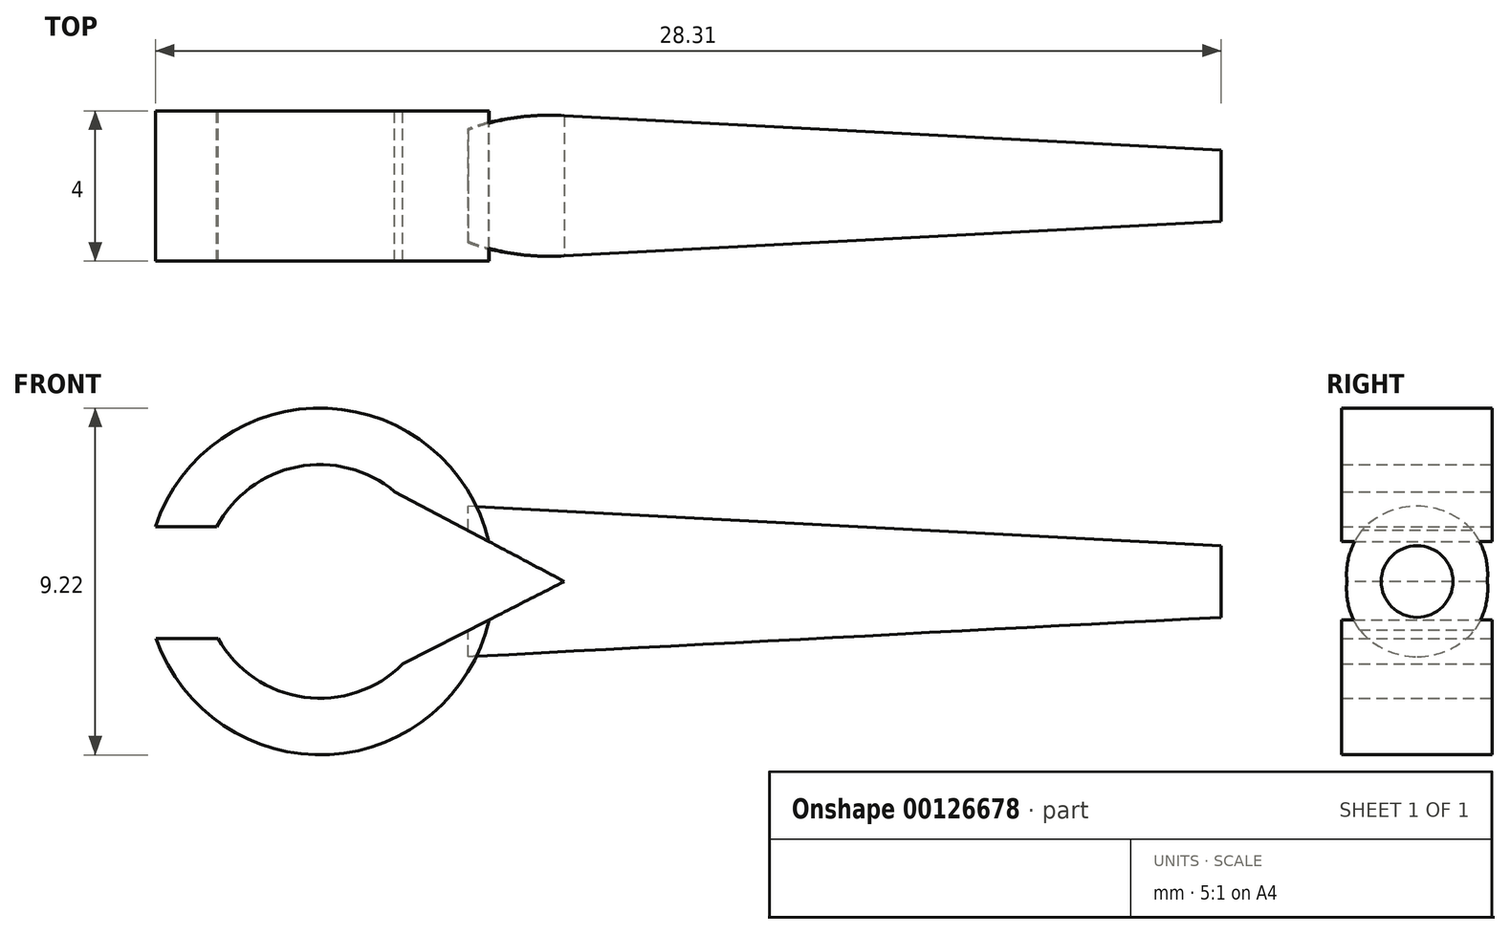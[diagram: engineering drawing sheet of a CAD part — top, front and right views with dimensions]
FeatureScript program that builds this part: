
annotation { "Feature Type Name" : "Feature", "Feature Type Description" : "" }
export const myFeature = defineFeature(function(context is Context, id is Id, definition is map)
    precondition{}
    {
        {
            var Q0;
            Q0=qCreatedBy(makeId("Front.planeOp"),FACE);
            var sketch = newSketch(context, id + "F0", { "sketchPlane" : qUnion([Q0])});
            skCircle(sketch, "E0", {"center": v(0, 0) * mm, "radius": 4.6 * mm});
            skCircle(sketch, "E1", {"center": v(0, 0) * mm, "radius": 3.1 * mm});
            skSolve(sketch);
        }
        {
            var Q0;
            Q0=makeQuery(id+"F0.imprint","IMPRINT",FACE,{"disambiguationData":[TD([[makeQuery(id+"F0.imprint","IMPRINT",EDGE,{"derivedFrom":sQuery(id+"F0.wireOp",EDGE,"E0")}),1.0]])]});
            extrude(context, id + "F1", {"entities" : qUnion([Q0]), "depth" : 4 * mm});
        }
        {
            var Q0;
            Q0=qCreatedBy(makeId("Right.planeOp"),FACE);
            var sketch = newSketch(context, id + "F2", { "sketchPlane" : qUnion([Q0])});
            skCircle(sketch, "E2", {"center": v(0, 0) * mm, "radius": 2 * mm});
            skSolve(sketch);
        }
        {
            var Q0;
            Q0 = qSketchRegion(id + "F2", true);
            extrude(context, id + "F3", {"entities" : qUnion([Q0]), "depth" : 20 * mm, "hasDraft" : true, "draftAngle" : 3 * degree, "draftPullDirection" : true});
        }
        {
            var Q0;
            Q0=makeQuery(id+"F3.opExtrude","SWEPT_BODY",BODY,{"disambiguationData":[OSD([sQuery(id+"F2.wireOp",EDGE,"E2")])]});
            transform(context, id + "F4", {"entities" : qUnion([Q0]), "transformType" : TransformType.TRANSLATION_3D, "dx" : 3.94 * mm, "dy" : -2 * mm, "dz" : 0 * mm, "makeCopy" : false});
        }
        {
            var Q0;
            Q0=makeQuery(id+"F1.opExtrude","CAP_FACE",FACE,{"disambiguationData":[OSD([sQuery(id+"F0.wireOp",EDGE,"E0"),sQuery(id+"F0.wireOp",EDGE,"E1")])],"isStart":false});
            cPlane(context, id + "F5", {"entities" : qUnion([Q0]), "cplaneType" : CPlaneType.OFFSET, "offset" : 1 * mm, "width" : 150 * mm, "height" : 150 * mm});
        }
        {
            var Q0;
            Q0=qCreatedBy(id+"F5.planeOp",FACE);
            var sketch = newSketch(context, id + "F6", { "sketchPlane" : qUnion([Q0])});
            skLineSegment(sketch, "E3", {"start": v(6.5, 0) * mm, "end": v(1.19, 2.8) * mm});
            skLineSegment(sketch, "E4", {"start": v(6.5, 0) * mm, "end": v(1.15, -2.73) * mm});
            skLineSegment(sketch, "E5", {"start": v(1.19, 2.8) * mm, "end": v(1.15, -2.73) * mm});
            skLineSegment(sketch, "E6.bottom", {"start": v(1.18, 1.45) * mm, "end": v(-4.84, 1.45) * mm});
            skLineSegment(sketch, "E6.top", {"start": v(1.18, -1.52) * mm, "end": v(-4.84, -1.52) * mm});
            skLineSegment(sketch, "E6.left", {"start": v(1.18, 1.45) * mm, "end": v(1.18, -1.52) * mm});
            skLineSegment(sketch, "E6.right", {"start": v(-4.84, 1.45) * mm, "end": v(-4.84, -1.52) * mm});
            skSolve(sketch);
        }
        {
            var Q0;
            Q0 = qSketchRegion(id + "F6", true);
            extrude(context, id + "F7", {"entities" : qUnion([Q0]), "operationType" : NewBodyOperationType.REMOVE, "oppositeDirection" : true, "depth" : 5 * mm});
        }
        {
            var Q0;
            Q0 = qSketchRegion(id + "F6", true);
            extrude(context, id + "F8", {"entities" : qUnion([Q0]), "operationType" : NewBodyOperationType.REMOVE, "oppositeDirection" : true, "depth" : 25 * mm});
        }
    });
